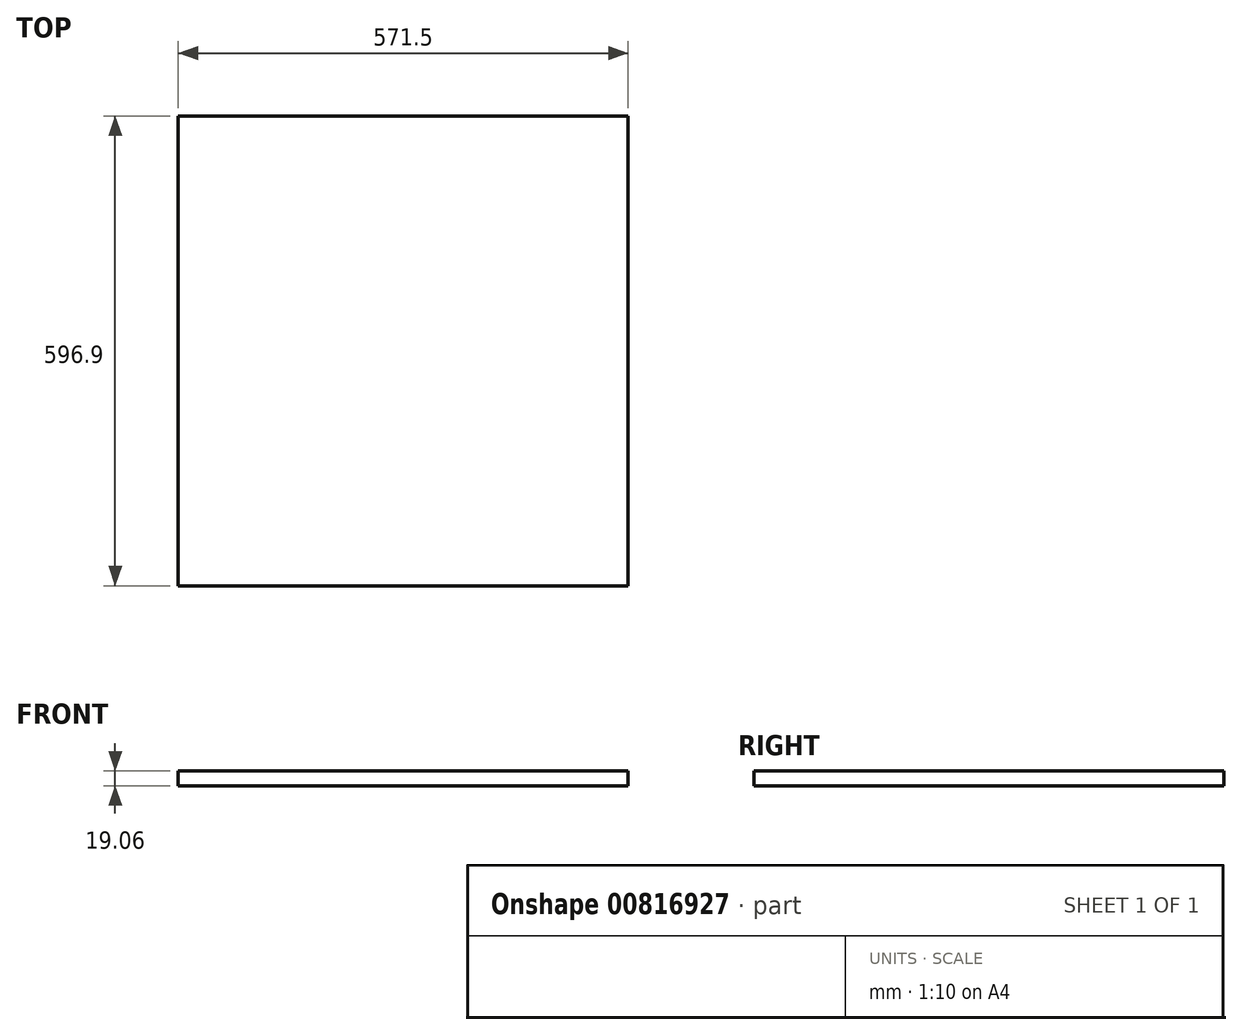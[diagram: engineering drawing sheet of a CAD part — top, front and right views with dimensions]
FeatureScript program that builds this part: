
annotation { "Feature Type Name" : "Feature", "Feature Type Description" : "" }
export const myFeature = defineFeature(function(context is Context, id is Id, definition is map)
    precondition{}
    {
        {
            var Q0;
            Q0=qCreatedBy(makeId("Top.planeOp"),FACE);
            var sketch = newSketch(context, id + "F0", { "sketchPlane" : qUnion([Q0])});
            skLineSegment(sketch, "E0.bottom", {"start": v(-285.75, -298.45) * mm, "end": v(285.75, -298.45) * mm});
            skLineSegment(sketch, "E0.top", {"start": v(-285.75, 298.45) * mm, "end": v(285.75, 298.45) * mm});
            skLineSegment(sketch, "E0.left", {"start": v(-285.75, -298.45) * mm, "end": v(-285.75, 298.45) * mm});
            skLineSegment(sketch, "E0.right", {"start": v(285.75, -298.45) * mm, "end": v(285.75, 298.45) * mm});
            skPoint(sketch, "E1", {"position": v(0, 298.45) * mm});
            skPoint(sketch, "E2", {"position": v(-285.75, 0) * mm});
            skSolve(sketch);
        }
        {
            var Q0;
            Q0=makeQuery(id+"F0.imprint","IMPRINT",FACE,{"disambiguationData":[TD([[makeQuery(id+"F0.imprint","IMPRINT",EDGE,{"derivedFrom":sQuery(id+"F0.wireOp",EDGE,"E0.bottom")}),1.0]])]});
            extrude(context, id + "F1", {"entities" : qUnion([Q0]), "endBound" : BoundingType.SYMMETRIC, "depth" : 19.05 * mm, "offsetDistance" : 25.4 * mm});
        }
    });
